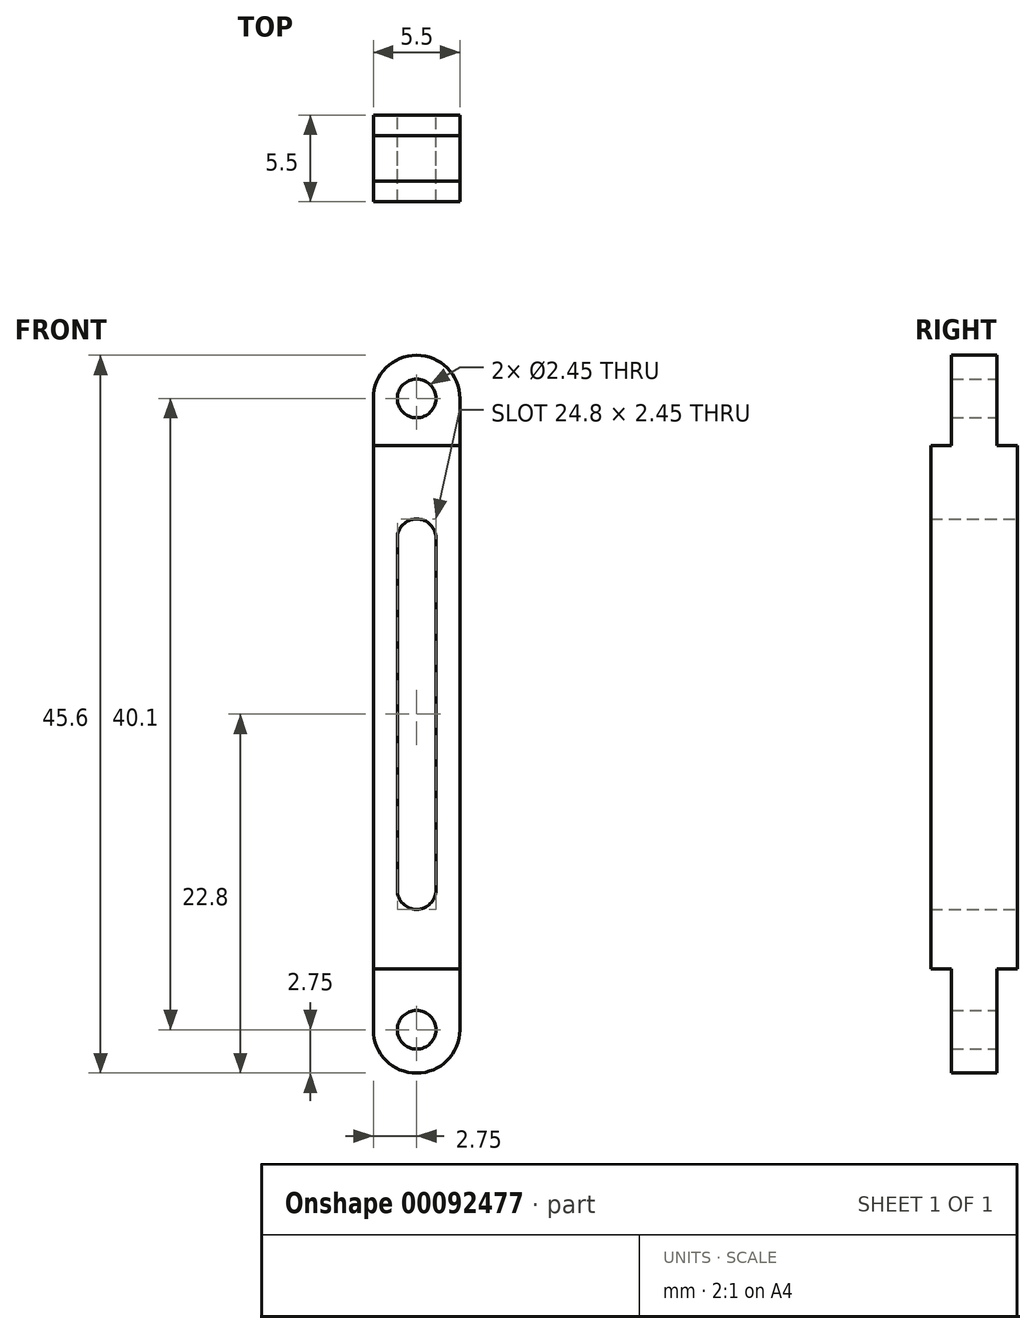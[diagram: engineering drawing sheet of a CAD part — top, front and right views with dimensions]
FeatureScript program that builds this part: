
annotation { "Feature Type Name" : "Feature", "Feature Type Description" : "" }
export const myFeature = defineFeature(function(context is Context, id is Id, definition is map)
    precondition{}
    {
        {
            var Q0;
            Q0=qCreatedBy(makeId("Front.planeOp"),FACE);
            var sketch = newSketch(context, id + "F0", { "sketchPlane" : qUnion([Q0])});
            skLineSegment(sketch, "E0.left", {"start": v(2.75, -20.05) * mm, "end": v(2.75, 20.05) * mm});
            skLineSegment(sketch, "E0.right", {"start": v(-2.75, -20.05) * mm, "end": v(-2.75, 20.05) * mm});
            skPoint(sketch, "E0.middle", {"position": v(0, 0) * mm});
            skArc(sketch, "E1", {"start": v(2.75, 20.05) * mm, "mid": v(0, 22.8) * mm, "end": v(-2.75, 20.05) * mm});
            skArc(sketch, "E2", {"start": v(-2.75, -20.05) * mm, "mid": v(0, -22.8) * mm, "end": v(2.75, -20.05) * mm});
            skCircle(sketch, "E3", {"center": v(0, -20.05) * mm, "radius": 1.23 * mm});
            skCircle(sketch, "E4", {"center": v(0, 20.05) * mm, "radius": 1.23 * mm});
            skLineSegment(sketch, "E5.left", {"start": v(-1.22, 11.18) * mm, "end": v(-1.22, -11.18) * mm});
            skLineSegment(sketch, "E5.right", {"start": v(1.23, 11.18) * mm, "end": v(1.23, -11.18) * mm});
            skArc(sketch, "E6", {"start": v(1.23, 11.18) * mm, "mid": v(0, 12.4) * mm, "end": v(-1.22, 11.18) * mm});
            skArc(sketch, "E7", {"start": v(-1.22, -11.18) * mm, "mid": v(0, -12.4) * mm, "end": v(1.23, -11.18) * mm});
            skSolve(sketch);
        }
        {
            var Q0;
            Q0 = qSketchRegion(id + "F0", true);
            extrude(context, id + "F1", {"entities" : qUnion([Q0]), "depth" : 5.5 * mm, "symmetric" : true});
        }
        {
            var Q0;
            Q0=makeQuery(id+"F0.imprint","IMPRINT",FACE,{"disambiguationData":[TD([[makeQuery(id+"F0.imprint","IMPRINT",EDGE,{"derivedFrom":sQuery(id+"F0.wireOp",EDGE,"E4")}),1.0]])]});
            var Q1;
            Q1=makeQuery(id+"F0.imprint","IMPRINT",FACE,{"disambiguationData":[TD([[makeQuery(id+"F0.imprint","IMPRINT",EDGE,{"derivedFrom":sQuery(id+"F0.wireOp",EDGE,"E5.left")}),1.0]])]});
            var Q2;
            Q2=makeQuery(id+"F0.imprint","IMPRINT",FACE,{"disambiguationData":[TD([[makeQuery(id+"F0.imprint","IMPRINT",EDGE,{"derivedFrom":sQuery(id+"F0.wireOp",EDGE,"E3")}),1.0]])]});
            extrude(context, id + "F2", {"entities" : qUnion([Q0, Q1, Q2]), "operationType" : NewBodyOperationType.REMOVE, "oppositeDirection" : true, "depth" : 25 * mm});
        }
        {
            var Q0;
            Q0=qCreatedBy(makeId("Right.planeOp"),FACE);
            var sketch = newSketch(context, id + "F3", { "sketchPlane" : qUnion([Q0])});
            skLineSegment(sketch, "E8.bottom", {"start": v(1.43, 17.07) * mm, "end": v(-1.42, 17.07) * mm, "construction": true});
            skLineSegment(sketch, "E8.left", {"start": v(1.43, 17.07) * mm, "end": v(1.43, 22.82) * mm, "construction": true});
            skLineSegment(sketch, "E8.right", {"start": v(-1.42, 17.07) * mm, "end": v(-1.42, 22.82) * mm, "construction": true});
            skPoint(sketch, "E8.middle", {"position": v(0, 19.95) * mm});
            skLineSegment(sketch, "E9.bottom", {"start": v(-1.44, 23.62) * mm, "end": v(-4.17, 23.62) * mm});
            skLineSegment(sketch, "E9.top", {"start": v(-1.44, 17.06) * mm, "end": v(-4.17, 17.06) * mm});
            skLineSegment(sketch, "E9.left", {"start": v(-1.44, 23.62) * mm, "end": v(-1.44, 17.06) * mm});
            skLineSegment(sketch, "E9.right", {"start": v(-4.17, 23.62) * mm, "end": v(-4.17, 17.06) * mm});
            skLineSegment(sketch, "E10.bottom", {"start": v(1.43, 23.62) * mm, "end": v(4.03, 23.62) * mm});
            skLineSegment(sketch, "E10.top", {"start": v(1.43, 17.06) * mm, "end": v(4.03, 17.06) * mm});
            skLineSegment(sketch, "E10.left", {"start": v(1.43, 23.62) * mm, "end": v(1.43, 17.06) * mm});
            skLineSegment(sketch, "E10.right", {"start": v(4.03, 23.62) * mm, "end": v(4.03, 17.06) * mm});
            skLineSegment(sketch, "E11.top", {"start": v(-1.43, -16.2) * mm, "end": v(1.43, -16.2) * mm, "construction": true});
            skLineSegment(sketch, "E11.left", {"start": v(-1.43, -22.75) * mm, "end": v(-1.43, -16.2) * mm, "construction": true});
            skLineSegment(sketch, "E11.right", {"start": v(1.43, -22.75) * mm, "end": v(1.43, -16.2) * mm, "construction": true});
            skLineSegment(sketch, "E12.bottom", {"start": v(-1.43, -16.2) * mm, "end": v(-4.25, -16.2) * mm});
            skLineSegment(sketch, "E12.top", {"start": v(-1.43, -23.36) * mm, "end": v(-4.25, -23.36) * mm});
            skLineSegment(sketch, "E12.left", {"start": v(-1.43, -16.2) * mm, "end": v(-1.43, -23.36) * mm});
            skLineSegment(sketch, "E12.right", {"start": v(-4.25, -16.2) * mm, "end": v(-4.25, -23.36) * mm});
            skLineSegment(sketch, "E13.bottom", {"start": v(1.43, -16.2) * mm, "end": v(4.02, -16.2) * mm});
            skLineSegment(sketch, "E13.top", {"start": v(1.43, -23.36) * mm, "end": v(4.02, -23.36) * mm});
            skLineSegment(sketch, "E13.left", {"start": v(1.43, -16.2) * mm, "end": v(1.43, -23.36) * mm});
            skLineSegment(sketch, "E13.right", {"start": v(4.02, -16.2) * mm, "end": v(4.02, -23.36) * mm});
            skSolve(sketch);
        }
        {
            var Q0;
            Q0 = qSketchRegion(id + "F3", true);
            extrude(context, id + "F4", {"entities" : qUnion([Q0]), "operationType" : NewBodyOperationType.REMOVE, "depth" : 10 * mm, "symmetric" : true});
        }
    });
